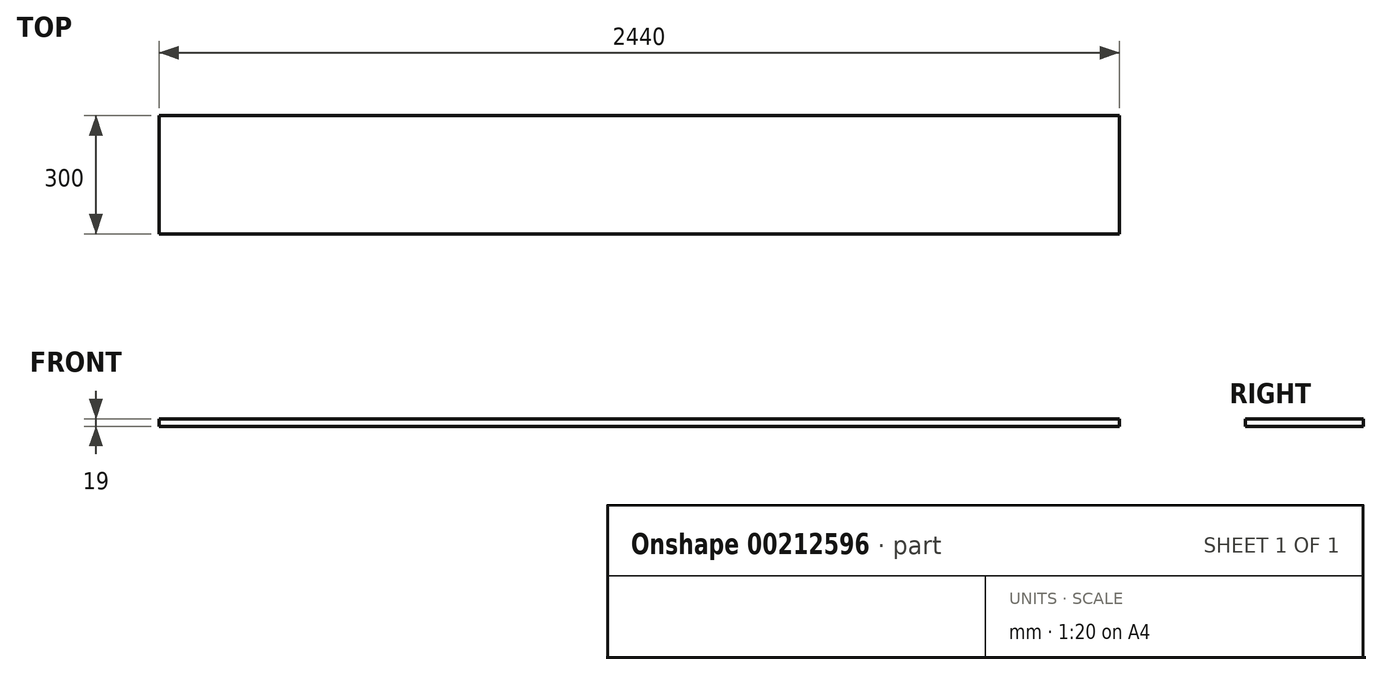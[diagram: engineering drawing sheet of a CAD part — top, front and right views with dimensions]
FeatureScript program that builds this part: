
annotation { "Feature Type Name" : "Feature", "Feature Type Description" : "" }
export const myFeature = defineFeature(function(context is Context, id is Id, definition is map)
    precondition{}
    {
        {
            var Q0;
            Q0=qCreatedBy(makeId("Top.planeOp"),FACE);
            var sketch = newSketch(context, id + "F0", { "sketchPlane" : qUnion([Q0])});
            skLineSegment(sketch, "E0.bottom", {"start": v(-1220, -150) * mm, "end": v(1220, -150) * mm});
            skLineSegment(sketch, "E0.top", {"start": v(-1220, 150) * mm, "end": v(1220, 150) * mm});
            skLineSegment(sketch, "E0.left", {"start": v(-1220, -150) * mm, "end": v(-1220, 150) * mm});
            skLineSegment(sketch, "E0.right", {"start": v(1220, -150) * mm, "end": v(1220, 150) * mm});
            skSolve(sketch);
        }
        {
            var Q0;
            Q0 = qSketchRegion(id + "F0", true);
            extrude(context, id + "F1", {"entities" : qUnion([Q0]), "depth" : 19 * mm});
        }
    });
